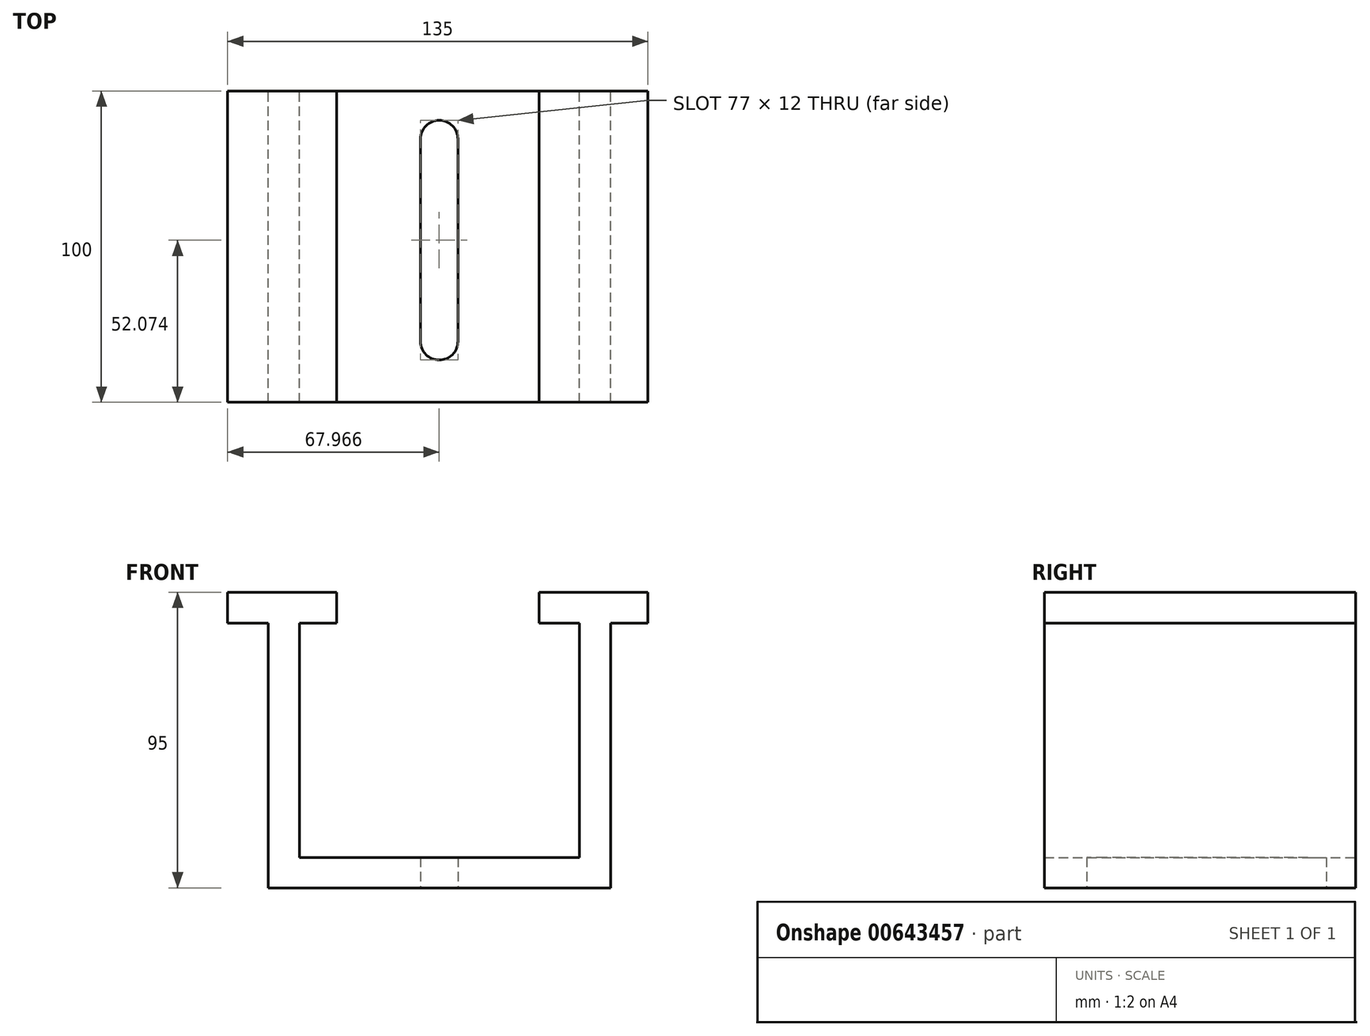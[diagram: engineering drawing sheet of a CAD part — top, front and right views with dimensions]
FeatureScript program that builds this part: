
annotation { "Feature Type Name" : "Feature", "Feature Type Description" : "" }
export const myFeature = defineFeature(function(context is Context, id is Id, definition is map)
    precondition{}
    {
        {
            var Q0;
            Q0=qCreatedBy(makeId("Front.planeOp"),FACE);
            var sketch = newSketch(context, id + "F0", { "sketchPlane" : qUnion([Q0])});
            skLineSegment(sketch, "E0.bottom", {"start": v(-72.64, 51.3) * mm, "end": v(-37.64, 51.3) * mm});
            skLineSegment(sketch, "E0.top", {"start": v(-72.64, 41.3) * mm, "end": v(-59.59, 41.3) * mm});
            skLineSegment(sketch, "E0.left", {"start": v(-72.64, 51.3) * mm, "end": v(-72.64, 41.3) * mm});
            skLineSegment(sketch, "E0.right", {"start": v(62.36, 51.3) * mm, "end": v(62.36, 41.3) * mm});
            skLineSegment(sketch, "E1.bottom", {"start": v(-59.59, 51.3) * mm, "end": v(-49.59, 51.3) * mm});
            skLineSegment(sketch, "E1.top", {"start": v(-59.59, -43.7) * mm, "end": v(-49.59, -43.7) * mm});
            skLineSegment(sketch, "E1.left", {"start": v(-59.59, 41.3) * mm, "end": v(-59.59, -43.7) * mm});
            skLineSegment(sketch, "E1.right", {"start": v(-49.59, 41.3) * mm, "end": v(-49.59, -33.98) * mm});
            skLineSegment(sketch, "E2.bottom", {"start": v(-59.59, -43.7) * mm, "end": v(50.41, -43.7) * mm});
            skLineSegment(sketch, "E2.top", {"start": v(-49.59, -33.98) * mm, "end": v(40.41, -33.98) * mm});
            skLineSegment(sketch, "E2.left", {"start": v(-59.59, -43.7) * mm, "end": v(-59.59, -33.98) * mm});
            skLineSegment(sketch, "E2.right", {"start": v(50.41, -43.7) * mm, "end": v(50.41, -33.98) * mm});
            skLineSegment(sketch, "E3.bottom", {"start": v(40.41, 51.3) * mm, "end": v(50.41, 51.3) * mm});
            skLineSegment(sketch, "E3.top", {"start": v(40.41, -43.7) * mm, "end": v(50.41, -43.7) * mm});
            skLineSegment(sketch, "E3.left", {"start": v(40.41, 41.3) * mm, "end": v(40.41, -33.98) * mm});
            skLineSegment(sketch, "E3.right", {"start": v(50.41, 41.3) * mm, "end": v(50.41, -43.7) * mm});
            skLineSegment(sketch, "E4", {"start": v(40.41, 51.3) * mm, "end": v(27.36, 51.3) * mm});
            skLineSegment(sketch, "E5", {"start": v(27.36, 51.3) * mm, "end": v(27.36, 41.3) * mm});
            skLineSegment(sketch, "E6", {"start": v(27.36, 41.3) * mm, "end": v(40.41, 41.3) * mm});
            skLineSegment(sketch, "E7", {"start": v(-37.64, 51.3) * mm, "end": v(-37.64, 41.3) * mm});
            skLineSegment(sketch, "E8", {"start": v(27.36, 51.3) * mm, "end": v(62.36, 51.3) * mm});
            skLineSegment(sketch, "E9", {"start": v(62.36, 41.3) * mm, "end": v(50.41, 41.3) * mm});
            skLineSegment(sketch, "E10.trimOffspring", {"start": v(-49.59, 41.3) * mm, "end": v(-37.64, 41.3) * mm});
            skLineSegment(sketch, "E11.trimOffspring", {"start": v(40.41, 41.3) * mm, "end": v(27.36, 41.3) * mm});
            skLineSegment(sketch, "E12.trimOffspring", {"start": v(50.41, 41.3) * mm, "end": v(62.36, 41.3) * mm});
            skSolve(sketch);
        }
        {
            var Q0;
            Q0 = qSketchRegion(id + "F0", true);
            extrude(context, id + "F1", {"entities" : qUnion([Q0]), "depth" : 100 * mm, "offsetDistance" : 25 * mm});
        }
        {
            var Q0;
            Q0=makeQuery(id+"F1.opExtrude","SWEPT_FACE",FACE,{"disambiguationData":[OSD([sQuery(id+"F0.wireOp",EDGE,"E2.bottom"),sQuery(id+"F0.wireOp",EDGE,"E3.top")])]});
            var sketch = newSketch(context, id + "F2", { "sketchPlane" : qUnion([Q0])});
            skPoint(sketch, "E13.end.orphan", {"position": v(0, 80.43) * mm});
            skLineSegment(sketch, "E14.left", {"start": v(-10.67, 80.43) * mm, "end": v(-10.67, 15.43) * mm});
            skLineSegment(sketch, "E14.right", {"start": v(1.33, 80.43) * mm, "end": v(1.33, 15.43) * mm});
            skPoint(sketch, "E15.orphan", {"position": v(-4.59, 100) * mm});
            skPoint(sketch, "E16.start.orphan", {"position": v(-4.59, 0) * mm});
            skArc(sketch, "E17", {"start": v(1.33, 80.43) * mm, "mid": v(-4.67, 86.43) * mm, "end": v(-10.67, 80.43) * mm});
            skArc(sketch, "E18", {"start": v(-10.67, 15.43) * mm, "mid": v(-4.67, 9.43) * mm, "end": v(1.33, 15.43) * mm});
            skSolve(sketch);
        }
        {
            var Q0;
            Q0 = qSketchRegion(id + "F2", true);
            extrude(context, id + "F3", {"entities" : qUnion([Q0]), "operationType" : NewBodyOperationType.REMOVE, "oppositeDirection" : true, "depth" : 29 * mm, "offsetDistance" : 25 * mm});
        }
    });
